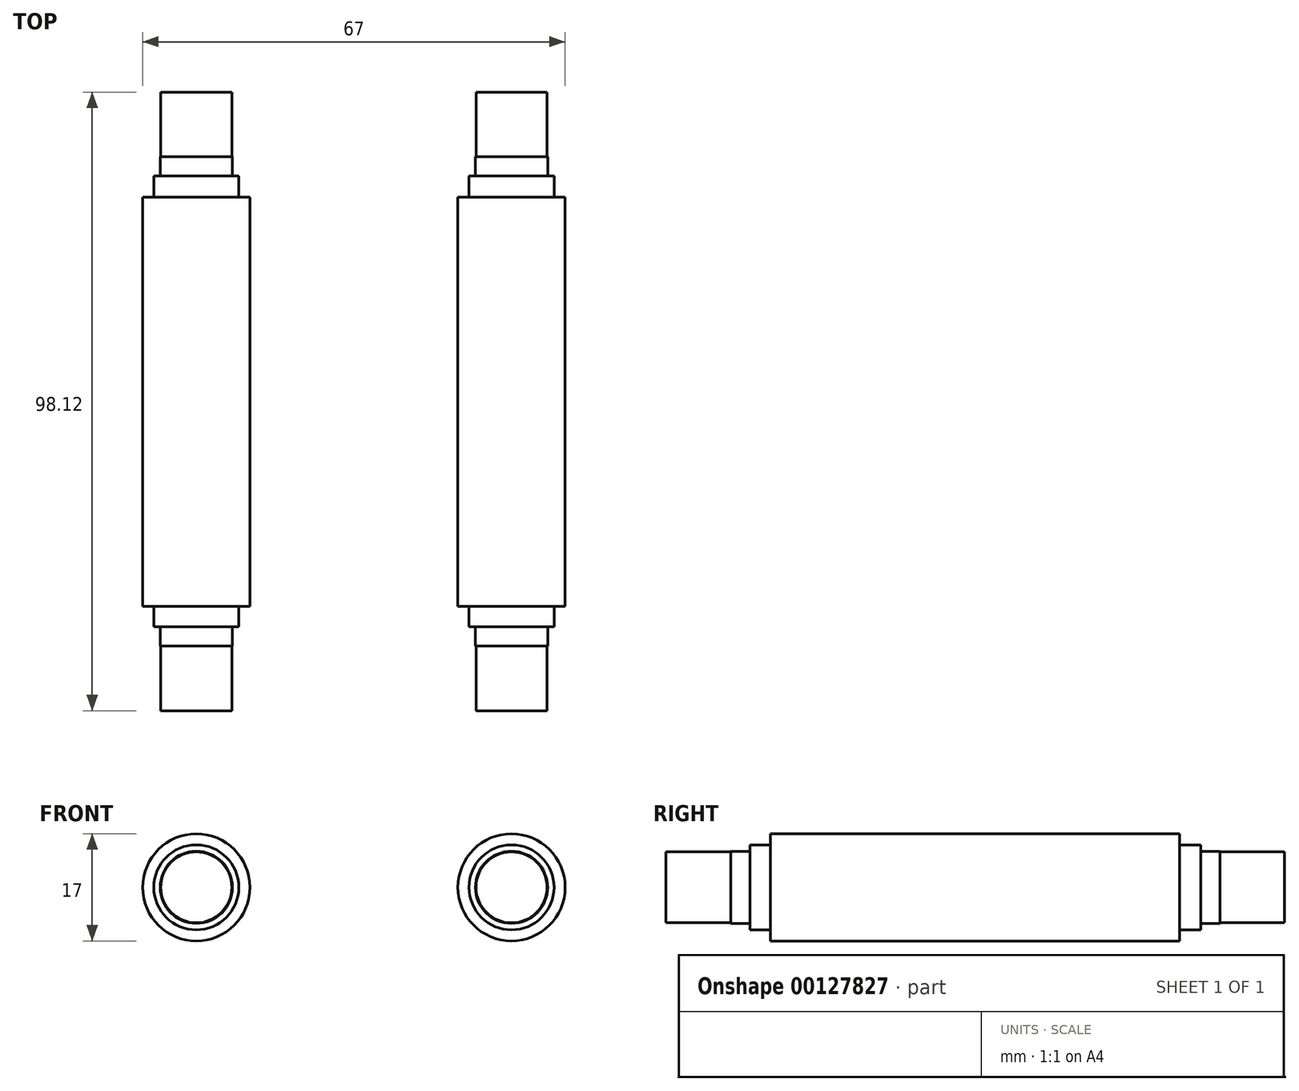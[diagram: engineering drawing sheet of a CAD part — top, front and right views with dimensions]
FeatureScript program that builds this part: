
annotation { "Feature Type Name" : "Feature", "Feature Type Description" : "" }
export const myFeature = defineFeature(function(context is Context, id is Id, definition is map)
    precondition{}
    {
        {
            var Q0;
            Q0=qCreatedBy(makeId("Front.planeOp"),FACE);
            var sketch = newSketch(context, id + "F0", { "sketchPlane" : qUnion([Q0])});
            skCircle(sketch, "E0", {"center": v(0, 0) * mm, "radius": 8.5 * mm});
            skSolve(sketch);
        }
        {
            var Q0;
            Q0 = qSketchRegion(id + "F0", true);
            extrude(context, id + "F1", {"entities" : qUnion([Q0]), "endBound" : BoundingType.SYMMETRIC, "depth" : 64.89 * mm});
        }
        {
            var Q0;
            Q0=makeQuery(id+"F1.opExtrude","CAP_FACE",FACE,{"disambiguationData":[OSD([sQuery(id+"F0.wireOp",EDGE,"E0")])],"isStart":false});
            var sketch = newSketch(context, id + "F2", { "sketchPlane" : qUnion([Q0])});
            skCircle(sketch, "E1", {"center": v(0, 0) * mm, "radius": 6.74 * mm});
            skSolve(sketch);
        }
        {
            var Q0;
            Q0 = qSketchRegion(id + "F2", true);
            extrude(context, id + "F3", {"entities" : qUnion([Q0]), "operationType" : NewBodyOperationType.ADD, "depth" : 3.28 * mm});
        }
        {
            var Q0;
            Q0=makeQuery(id+"F3.opExtrude","CAP_FACE",FACE,{"disambiguationData":[OSD([sQuery(id+"F2.wireOp",EDGE,"E1")])],"isStart":false});
            var sketch = newSketch(context, id + "F4", { "sketchPlane" : qUnion([Q0])});
            skCircle(sketch, "E2", {"center": v(0, 0) * mm, "radius": 5.73 * mm});
            skSolve(sketch);
        }
        {
            var Q0;
            Q0 = qSketchRegion(id + "F4", true);
            extrude(context, id + "F5", {"entities" : qUnion([Q0]), "operationType" : NewBodyOperationType.ADD, "depth" : 3.04 * mm});
        }
        {
            var Q0;
            Q0=makeQuery(id+"F5.opExtrude","CAP_FACE",FACE,{"disambiguationData":[OSD([sQuery(id+"F4.wireOp",EDGE,"E2")])],"isStart":false});
            var sketch = newSketch(context, id + "F6", { "sketchPlane" : qUnion([Q0])});
            skCircle(sketch, "E3", {"center": v(0, 0) * mm, "radius": 5.63 * mm});
            skSolve(sketch);
        }
        {
            var Q0;
            Q0 = qSketchRegion(id + "F6", true);
            extrude(context, id + "F7", {"entities" : qUnion([Q0]), "operationType" : NewBodyOperationType.ADD, "depth" : 10.25 * mm});
        }
        {
            var Q0;
            Q0=makeQuery(id+"F1.opExtrude","CAP_FACE",FACE,{"disambiguationData":[OSD([sQuery(id+"F0.wireOp",EDGE,"E0")])],"isStart":true});
            var sketch = newSketch(context, id + "F8", { "sketchPlane" : qUnion([Q0])});
            skCircle(sketch, "E4", {"center": v(0, 0) * mm, "radius": 6.74 * mm});
            skSolve(sketch);
        }
        {
            var Q0;
            Q0 = qSketchRegion(id + "F8", true);
            extrude(context, id + "F9", {"entities" : qUnion([Q0]), "operationType" : NewBodyOperationType.ADD, "depth" : 3.36 * mm});
        }
        {
            var Q0;
            Q0=makeQuery(id+"F9.opExtrude","CAP_FACE",FACE,{"disambiguationData":[OSD([sQuery(id+"F8.wireOp",EDGE,"E4")])],"isStart":false});
            var sketch = newSketch(context, id + "F10", { "sketchPlane" : qUnion([Q0])});
            skCircle(sketch, "E5", {"center": v(0, 0) * mm, "radius": 5.73 * mm});
            skSolve(sketch);
        }
        {
            var Q0;
            Q0 = qSketchRegion(id + "F10", true);
            extrude(context, id + "F11", {"entities" : qUnion([Q0]), "operationType" : NewBodyOperationType.ADD, "depth" : 3.04 * mm});
        }
        {
            var Q0;
            Q0=makeQuery(id+"F11.opExtrude","CAP_FACE",FACE,{"disambiguationData":[OSD([sQuery(id+"F10.wireOp",EDGE,"E5")])],"isStart":false});
            var sketch = newSketch(context, id + "F12", { "sketchPlane" : qUnion([Q0])});
            skCircle(sketch, "E6", {"center": v(0, 0) * mm, "radius": 5.63 * mm});
            skSolve(sketch);
        }
        {
            var Q0;
            Q0 = qSketchRegion(id + "F12", true);
            extrude(context, id + "F13", {"entities" : qUnion([Q0]), "operationType" : NewBodyOperationType.ADD, "depth" : 10.25 * mm});
        }
        {
            var Q0;
            Q0=qCreatedBy(makeId("Right.planeOp"),FACE);
            cPlane(context, id + "F14", {"entities" : qUnion([Q0]), "cplaneType" : CPlaneType.OFFSET, "offset" : 25 * mm, "width" : 150 * mm, "height" : 150 * mm});
        }
        {
            var Q0;
            Q0=makeQuery(id+"F1.opExtrude","SWEPT_BODY",BODY,{"disambiguationData":[OSD([sQuery(id+"F0.wireOp",EDGE,"E0")])]});
            var Q1;
            Q1=qCreatedBy(id+"F14.planeOp",FACE);
            mirror(context, id + "F15", {"entities" : qUnion([Q0]), "mirrorPlane" : qUnion([Q1])});
        }
    });
